# Revit family: SU-300-G_GENERADO
name_source: partatom
category: Equipos mecánicos
revit_build: Autodesk Revit 2014 (Build: 20130308_1515(x64)
units: mm (PartAtom-declared; Revit-internal decimal feet)

## types (14) — shared parameters
Depth = 465 mm  [stored 1.52559 ft]
Fabricante = SAMMIC S.L.
Foodservice Equipment Identifier = Sí
Height = 403 mm  [stored 1.32218 ft]
Revision Code = 1
URL = https://www.sammic.com
URL Cutsheet = http://www.sammic.com
Weight in Pounds = 75
Width = 384 mm  [stored 1.25984 ft]

## per-type parameters (varying)
| type | Comentarios de tipo | Cycle | FL Amps | Modelo | Specification by Manufacturer | Volts |
| Vacuum packing machine SU-310G 230/50-60/1 | Tabletop model. 10 m³/h. 320 mm. | 50 Hz | 3 A | 1140731 | 320 mm. sealing bar.
10 m³/h Busch vacuum pump.
Vacuum controlled by sensor. | 230 V |
| Vacuum packing machine SU-310GP 230/50-60/1 | Tabletop model. 10 m³/h. 320 mm. | 50 Hz | 3 A | 1140733 | 320 mm. sealing bar.
10 m³/h Busch vacuum pump.
Vacuum controlled by sensor. | 230 V |
| Vacuum packing machine SU-310G 120/50-60/1 | Tabletop model. 10 m³/h. 320 mm. | 60 Hz | 6 A | 1140736 | 320 mm. sealing bar.
10 m³/h Busch vacuum pump.
Vacuum controlled by sensor. | 120 V |
| Vacuum packing machine SU-310GP 120/50-60/1 | Tabletop model. 10 m³/h. 320 mm. | 60 Hz | 6 A | 1140738 | 320 mm. sealing bar.
10 m³/h Busch vacuum pump.
Vacuum controlled by sensor. | 120 V |
| Vacuum packing machine SU-310G+ 120/50-60/1 | Tabletop model. 10 m³/h. 320 mm. | 60 Hz | 6 A | 1140739 | 320 mm. sealing bar.
10 m³/h Busch vacuum pump.
Vacuum controlled by sensor. | 120 V |
| Vacuum packing machine SU-310GP+ 120/60/1 | Tabletop model. 10 m³/h. 320 mm. | 60 Hz | 6 A | 1140740 | 320 mm. sealing bar.
10 m³/h Busch vacuum pump.
Vacuum controlled by sensor. | 120 V |
| Vacuum packing machine SU-316G 230/50-60/1 | Tabletop model. 16 m³/h. 320 mm. | 50 Hz | 4 A | 1140743 | 320 mm. sealing bar.
16 m³/h Busch vacuum pump.
Vacuum controlled by sensor. | 230 V |
| Vacuum packing machine SU-316GP 230/50-60/1 | Tabletop model. 16 m³/h. 320 mm. | 50 Hz | 4 A | 1140747 | 320 mm. sealing bar.
16 m³/h Busch vacuum pump.
Vacuum controlled by sensor. | 230 V |
| Vacuum packing machine SU-316G+ 230/50-60/1 | Tabletop model. 16 m³/h. 320 mm. | 50 Hz | 4 A | 1140748 | 320 mm. sealing bar.
16 m³/h Busch vacuum pump.
Vacuum controlled by sensor. | 230 V |
| Vacuum packing machine SU-316GP+ 230/50-60/1 | Tabletop model. 16 m³/h. 320 mm. | 50 Hz | 4 A | 1140749 | 320 mm. sealing bar.
16 m³/h Busch vacuum pump.
Vacuum controlled by sensor. | 230 V |
| Vacuum packing machine SU-316G 120/50-60/1 | Tabletop model. 16 m³/h. 320 mm. | 60 Hz | 8 A | 1140752 | 320 mm. sealing bar.
16 m³/h Busch vacuum pump.
Vacuum controlled by sensor. | 120 V |
| Vacuum packing machine SU-316GP 120/50-60/1 | Tabletop model. 16 m³/h. 320 mm. | 60 Hz | 8 A | 1140756 | 320 mm. sealing bar.
16 m³/h Busch vacuum pump.
Vacuum controlled by sensor. | 120 V |
| Vacuum packing machine SU-316G+ 120/50-60/1 | Tabletop model. 16 m³/h. 320 mm. | 60 Hz | 8 A | 1140757 | 320 mm. sealing bar.
16 m³/h Busch vacuum pump.
Vacuum controlled by sensor. | 120 V |
| Vacuum packing machine SU-316GP+ 120/50-60/1 | Tabletop model. 16 m³/h. 320 mm. | 60 Hz | 8 A | 1140758 | 320 mm. sealing bar.
16 m³/h Busch vacuum pump.
Vacuum controlled by sensor. | 120 V |

note: column(s) folded — value = type name in every type: Descripción

note: [stored X ft] marks values corroborated as IEEE doubles in the binary element streams (Revit-internal decimal feet)

## geometry (parser evidence)
native form markers: Sweep x3
no freeform markers — native parametric forms only
